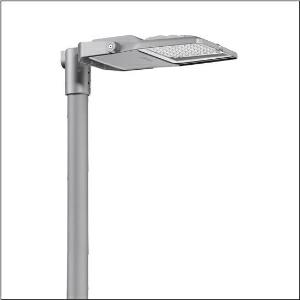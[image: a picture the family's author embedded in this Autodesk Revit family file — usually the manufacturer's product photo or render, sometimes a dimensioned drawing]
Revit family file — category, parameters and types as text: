
# Revit family: floodlight_fl_21_iq_mini___pl43_5xa7771d4a3a_2bc1
name_source: partatom
category: Lighting Fixtures
units: mm (PartAtom-declared; Revit-internal decimal feet)

## family parameters
Cut with Voids When Loaded = No
Host = Face
Light Source = No
Part Type = Normal
Room Calculation Point = No
Round Connector Dimension = Use Diameter
Shared = No

## types (1)
- --- (1 x LED, 19090 lm, 143 W, 4000K)
    Apparent Load = 143 VA
    CIE Flux Codes = 27 78 99 100 100
    Color Rendering = 70
    Color Temperature = 4000K
    Default Elevation = 1800 mm
    Description = Floodlight FL 21 iQ mini, floodlight, primary light control with lens, of PMMA, primary optical cover: protective disc, of toughened safety glass, transparent, light distribution: PL43, light emission: direct distribution, installation type: surface-mounted, LED, High Power LED, rated luminous flux: 19.090lm, luminous efficacy: 134lm/W, light colour: 740, colour temperature: 4000K, control: Auto-Match, Temp-Guard, Lumen-Switch, Night-Set, Smart-Wire, Light-Fading, Desk-Remote (wireless, voltage-free reading and setting of iQ features in the workshop via application-optimized NFC function/RFID function), optimised constant luminous flux control (CLO 2.0), with terminal, 6-pole, mains connection: 220..240V, AC, 50/60Hz, start of lifetime: 143W, end of service life: 152W, reduction: 61W, luminaire housing, of diecast aluminium, powder-coated, Siteco® metallic grey (DB 702S), corrosivity category C5 mid according to DIN EN ISO 12944, sealing non-destructively replaceable, please order mast flange separately, mast bracket, of steel, galvanised, powder-coated, Siteco® metallic grey (DB 702S), protection rating (complete): IP66, insulation class (complete): insulation class II (safety insulation), certification: CE, ENEC, VDE, protection symbol: D, impact resistance: IK08, permissible operating ambient temperature: -40..+40°C, permissible operating ambient temperature for outdoor applications: -40..+50°C, standard: DIN EN 12944, LABS conformity tested according to VDMA 24364:2018-05, packaging unit: 1 piece

Light Distribution: PL43
    Height = 70 mm
    Lamp = 1 x LED
    Lamp Light Flux = 19090 lm
    Lamp Power = 143 W
    Lamp count = 1
    Length = 485 mm
    Luminous efficacy = 133 lm/W
    Manufacturer = Siteco
    ModVariant = No
    Model = 5XA7771D4A3A
    Number of Poles = 1
    OnlyDefault = Yes
    Power Factor = 1
    Product Name = Floodlight FL 21 iQ mini | PL43
    Product group = floodlight | pylon annexe
    ProductGroupID = 6200
    Protection Class = Protection class II
    Protection Degree = IP 66
    RLX_Detail_Level = 1
    RLX_Emergency_Light_Flux = 0 lm
    RLX_Emergency_Type = 0
    RLX_Emergency_Type_DB = No
    RlxData = <blob elided: 101453 chars, md5=07bcedf6>
    Socket = socket
    Standby Power = 0 W
    System Light Flux = 19090 lm
    System Power = 143 W
    Type Comments = factory setting: luminous flux: 100 % | dim-lin: 254 | 730 mA
    Type Image = l_1007125.jpg
    URL = http://relux.com
    VarID = @adj_132087
    Voltage = 0 V
    Weight = 0.00 kg
    Width = 337 mm

## geometry (parser evidence)
native form markers: Blend x4, Sweep x14
no freeform markers — native parametric forms only
